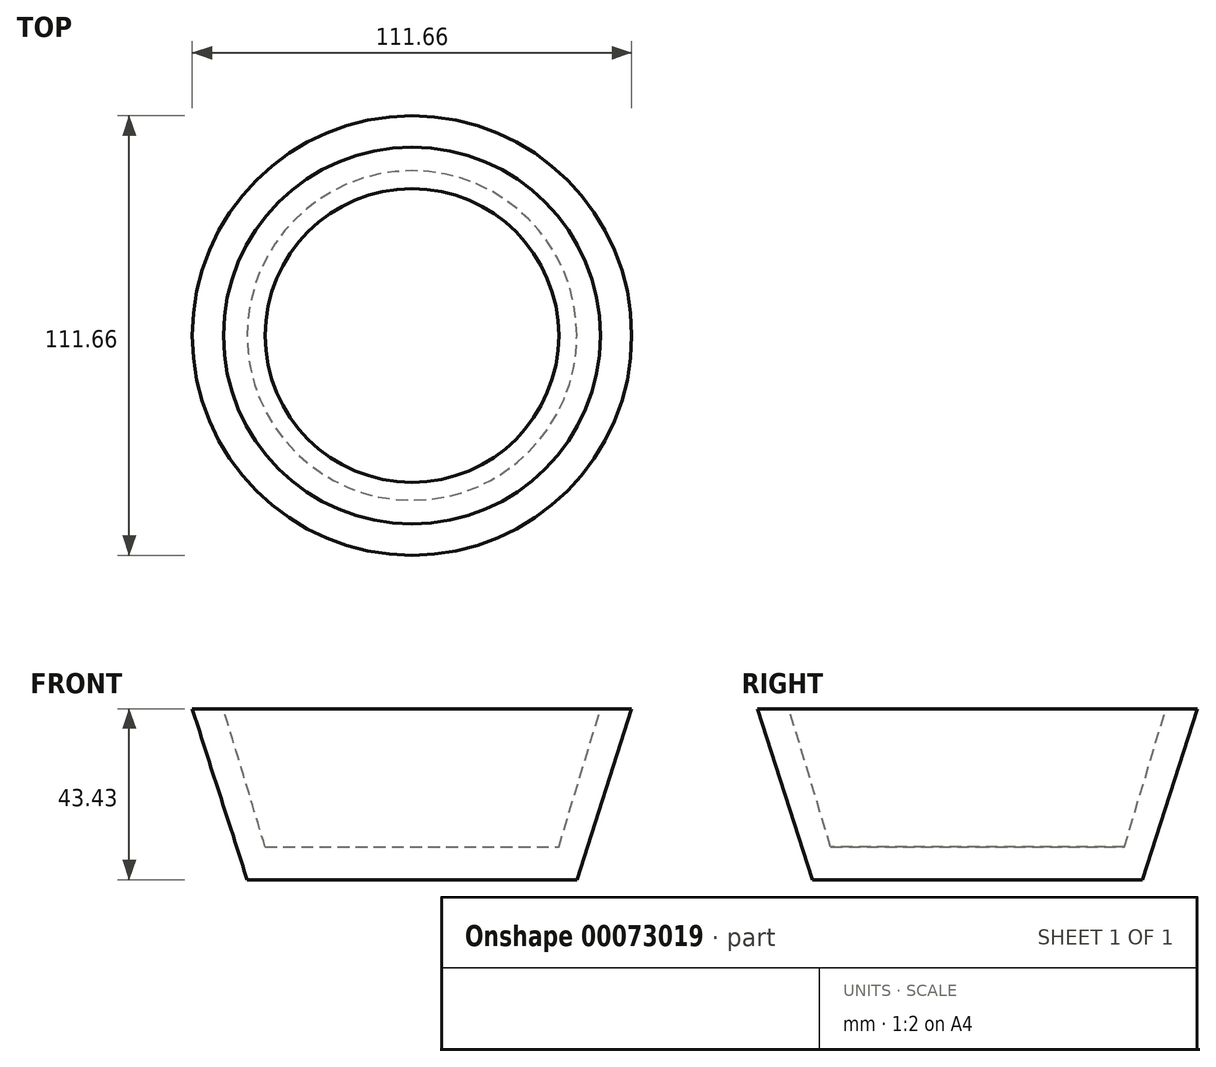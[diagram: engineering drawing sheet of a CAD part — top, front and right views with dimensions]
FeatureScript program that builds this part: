
annotation { "Feature Type Name" : "Feature", "Feature Type Description" : "" }
export const myFeature = defineFeature(function(context is Context, id is Id, definition is map)
    precondition{}
    {
        {
            var Q0;
            Q0=qCreatedBy(makeId("Front.planeOp"),FACE);
            var sketch = newSketch(context, id + "F0", { "sketchPlane" : qUnion([Q0])});
            skLineSegment(sketch, "E0", {"start": v(0, 0) * mm, "end": v(0, 8.3) * mm});
            skLineSegment(sketch, "E1", {"start": v(0, 8.3) * mm, "end": v(37.3, 8.3) * mm});
            skLineSegment(sketch, "E2", {"start": v(37.3, 8.3) * mm, "end": v(47.89, 43.43) * mm});
            skLineSegment(sketch, "E3", {"start": v(47.89, 43.43) * mm, "end": v(55.83, 43.43) * mm});
            skLineSegment(sketch, "E4", {"start": v(55.83, 43.43) * mm, "end": v(41.87, 0) * mm});
            skLineSegment(sketch, "E5", {"start": v(41.87, 0) * mm, "end": v(0, 0) * mm});
            skSolve(sketch);
        }
        {
            var Q0;
            Q0=makeQuery(id+"F0.imprint","IMPRINT",FACE,{"disambiguationData":[TD([[makeQuery(id+"F0.imprint","IMPRINT",EDGE,{"derivedFrom":sQuery(id+"F0.wireOp",EDGE,"E0")}),-1.0]])]});
            var Q1;
            Q1=sQuery(id+"F0.wireOp",EDGE,"E0");
            revolve(context, id + "F1", {"entities" : qUnion([Q0]), "axis" : qUnion([Q1]), "revolveType" : RevolveType.FULL});
        }
        {
            var Q0;
            Q0=makeQuery(id+"F0.imprint","IMPRINT",FACE,{"disambiguationData":[TD([[makeQuery(id+"F0.imprint","IMPRINT",EDGE,{"derivedFrom":sQuery(id+"F0.wireOp",EDGE,"E0")}),-1.0]])]});
            var Q1;
            Q1=sQuery(id+"F0.wireOp",EDGE,"E0");
            revolve(context, id + "F2", {"entities" : qUnion([Q0]), "axis" : qUnion([Q1]), "revolveType" : RevolveType.FULL});
        }
    });
